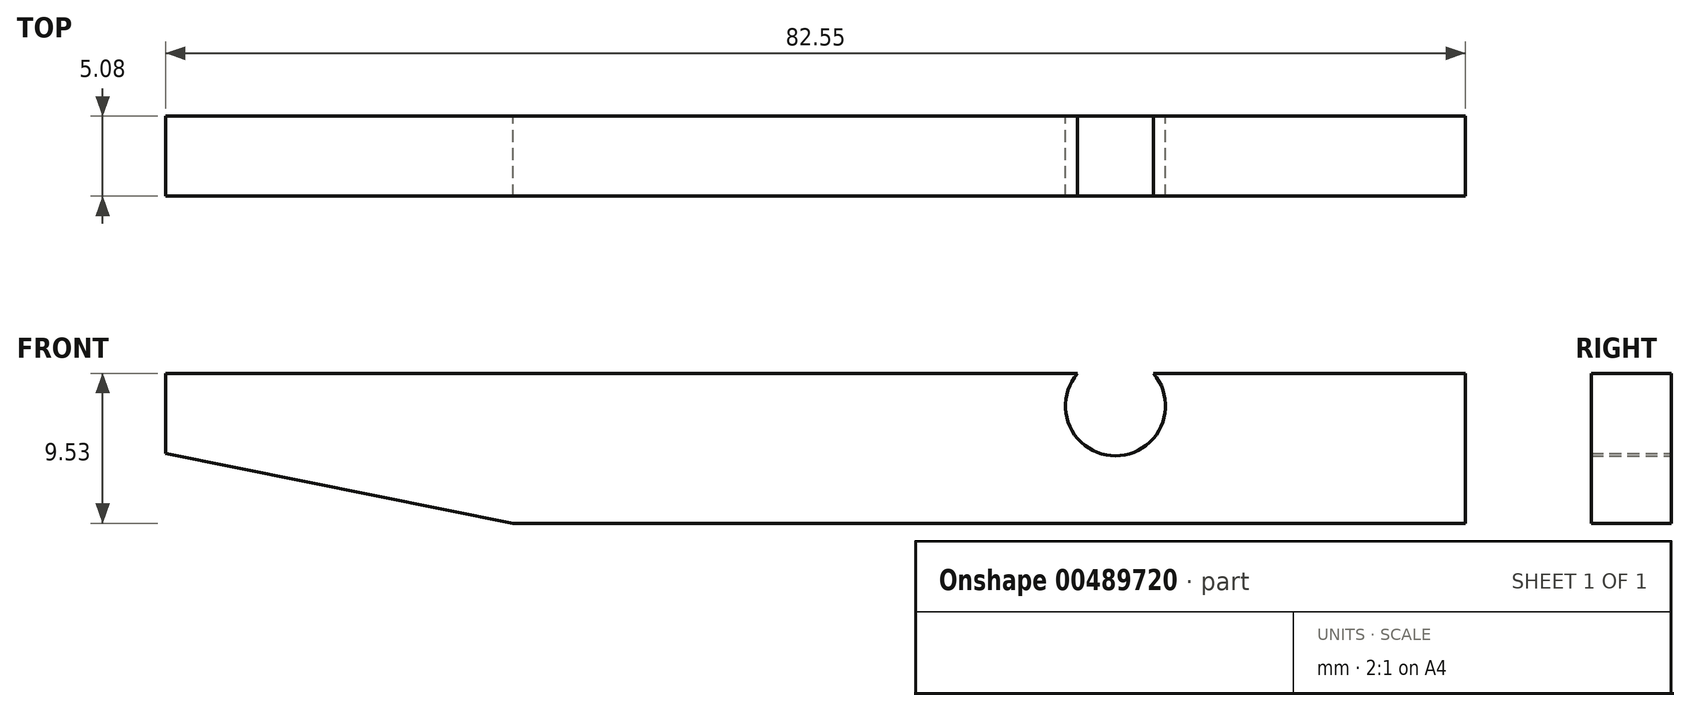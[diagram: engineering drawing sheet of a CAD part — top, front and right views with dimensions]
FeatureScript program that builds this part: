
annotation { "Feature Type Name" : "Feature", "Feature Type Description" : "" }
export const myFeature = defineFeature(function(context is Context, id is Id, definition is map)
    precondition{}
    {
        {
            var Q0;
            Q0=qCreatedBy(makeId("Front.planeOp"),FACE);
            var sketch = newSketch(context, id + "F0", { "sketchPlane" : qUnion([Q0])});
            skLineSegment(sketch, "E0.bottom", {"start": v(-51.79, 9.52) * mm, "end": v(2.19, 9.52) * mm});
            skLineSegment(sketch, "E0.top", {"start": v(-29.73, 0) * mm, "end": v(30.76, 0) * mm});
            skLineSegment(sketch, "E0.right", {"start": v(30.76, 9.52) * mm, "end": v(30.76, 0) * mm});
            skLineSegment(sketch, "E1", {"start": v(30.76, 9.52) * mm, "end": v(14.89, 9.52) * mm});
            skLineSegment(sketch, "E2.trimOffspring", {"start": v(14.89, 9.52) * mm, "end": v(30.76, 9.52) * mm});
            skPoint(sketch, "E3.orphan", {"position": v(-51.79, 1.27) * mm});
            skPoint(sketch, "E4.start.orphan", {"position": v(8.54, 0.85) * mm});
            skPoint(sketch, "E5.orphan", {"position": v(8.54, 4.61) * mm});
            skPoint(sketch, "E6.end.orphan", {"position": v(8.54, 4.44) * mm});
            skPoint(sketch, "E7.orphan", {"position": v(2.19, 9.52) * mm});
            skPoint(sketch, "E8.orphan", {"position": v(2.35, 9.52) * mm});
            skPoint(sketch, "E9.start.orphan", {"position": v(8.54, 3.17) * mm});
            skLineSegment(sketch, "E10", {"start": v(-51.79, 4.44) * mm, "end": v(-29.73, 0) * mm});
            skLineSegment(sketch, "E11", {"start": v(-51.79, 9.52) * mm, "end": v(-51.79, 4.44) * mm});
            skArc(sketch, "E12", {"start": v(6.12, 9.52) * mm, "mid": v(8.54, 4.29) * mm, "end": v(10.95, 9.52) * mm});
            skLineSegment(sketch, "E13", {"start": v(14.89, 9.52) * mm, "end": v(10.95, 9.52) * mm});
            skLineSegment(sketch, "E14", {"start": v(2.35, 9.52) * mm, "end": v(6.12, 9.52) * mm});
            skPoint(sketch, "E15.trimOffspring.end.orphan", {"position": v(8.54, 10.48) * mm});
            skPoint(sketch, "E16.orphan", {"position": v(-51.79, 0.81) * mm});
            skLineSegment(sketch, "E17", {"start": v(-51.79, 9.52) * mm, "end": v(6.12, 9.52) * mm});
            skLineSegment(sketch, "E18.trimOffspring", {"start": v(10.95, 9.52) * mm, "end": v(30.76, 9.52) * mm});
            skSolve(sketch);
        }
        {
            var Q0;
            Q0 = qSketchRegion(id + "F0", true);
            extrude(context, id + "F1", {"entities" : qUnion([Q0]), "depth" : 5.08 * mm});
        }
    });
